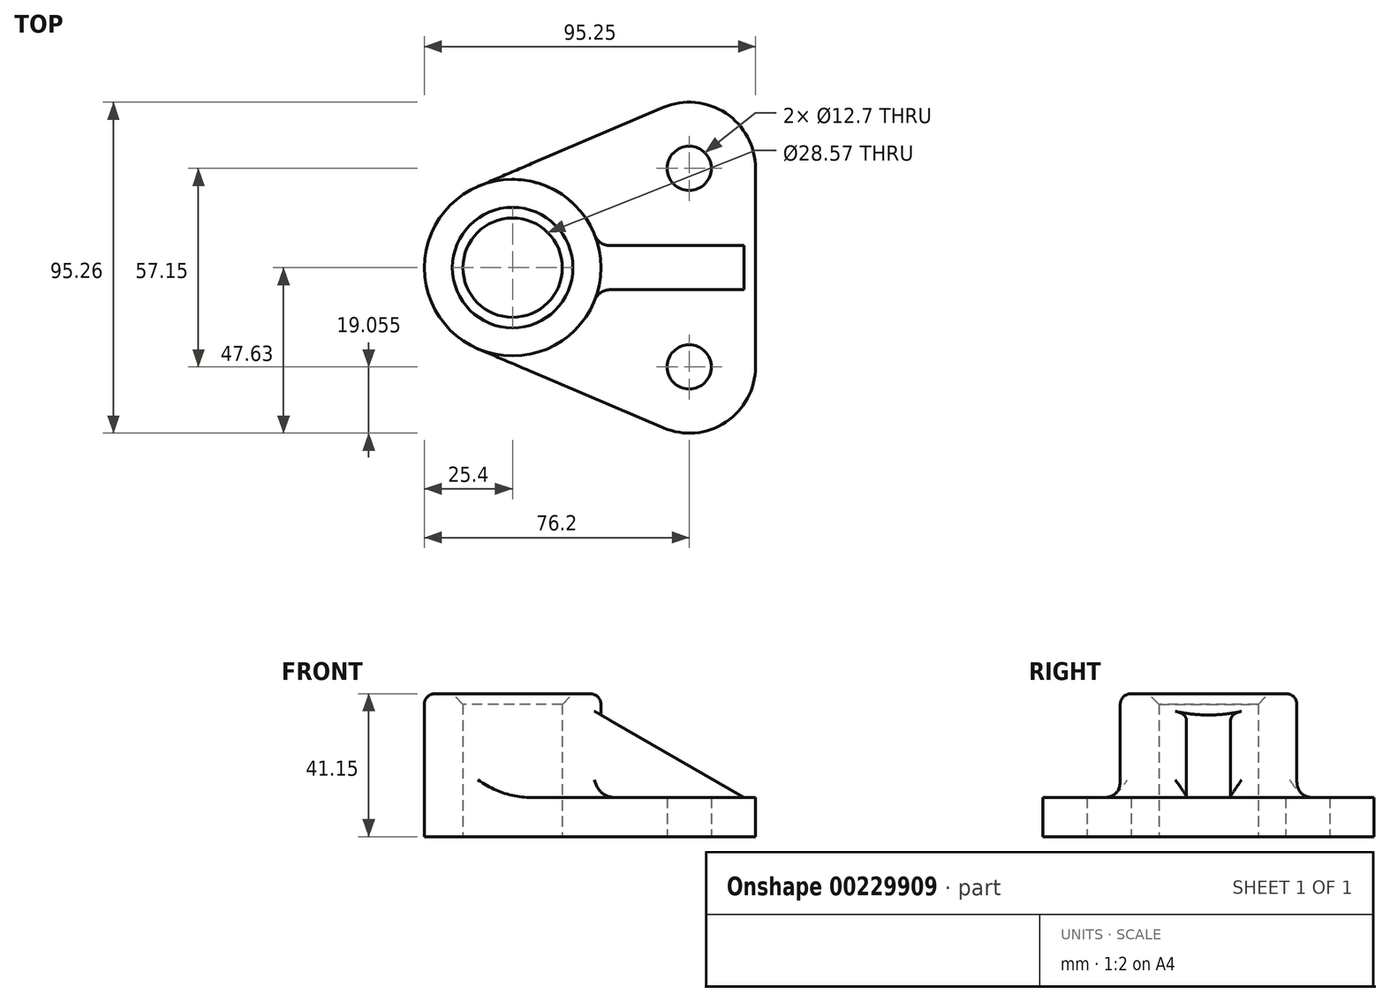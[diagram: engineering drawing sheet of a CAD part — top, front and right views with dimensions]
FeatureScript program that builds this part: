
annotation { "Feature Type Name" : "Feature", "Feature Type Description" : "" }
export const myFeature = defineFeature(function(context is Context, id is Id, definition is map)
    precondition{}
    {
        {
            var Q0;
            Q0=qCreatedBy(makeId("Top.planeOp"),FACE);
            var sketch = newSketch(context, id + "F0", { "sketchPlane" : qUnion([Q0])});
            skCircle(sketch, "E0", {"center": v(0, 0) * mm, "radius": 25.4 * mm});
            skCircle(sketch, "E1", {"center": v(0, 0) * mm, "radius": 14.29 * mm});
            skLineSegment(sketch, "E2", {"start": v(0, 0) * mm, "end": v(14.29, 0) * mm, "construction": true});
            skCircle(sketch, "E3", {"center": v(50.8, -28.58) * mm, "radius": 6.35 * mm});
            skCircle(sketch, "E4", {"center": v(50.8, 28.58) * mm, "radius": 6.35 * mm});
            skArc(sketch, "E5", {"start": v(69.85, 28.58) * mm, "mid": v(61.3, 44.47) * mm, "end": v(43.33, 46.1) * mm});
            skArc(sketch, "E6", {"start": v(43.33, -46.1) * mm, "mid": v(61.3, -44.47) * mm, "end": v(69.85, -28.58) * mm});
            skLineSegment(sketch, "E7", {"start": v(-9.97, 23.36) * mm, "end": v(43.33, 46.1) * mm});
            skLineSegment(sketch, "E8", {"start": v(-9.97, -23.36) * mm, "end": v(43.33, -46.1) * mm});
            skLineSegment(sketch, "E9", {"start": v(69.85, -28.58) * mm, "end": v(69.85, 28.58) * mm});
            skPoint(sketch, "E10.orphan", {"position": v(48.26, 0) * mm});
            skSolve(sketch);
        }
        {
            var Q0;
            Q0 = qSketchRegion(id + "F0", true);
            extrude(context, id + "F1", {"entities" : qUnion([Q0]), "depth" : 11.28 * mm});
        }
        {
            var Q0;
            Q0=makeQuery(id+"F0.imprint","IMPRINT",FACE,{"disambiguationData":[TD([[makeQuery(id+"F0.imprint","IMPRINT",EDGE,{"derivedFrom":sQuery(id+"F0.wireOp",EDGE,"E1")}),-1.0]])]});
            extrude(context, id + "F2", {"entities" : qUnion([Q0]), "operationType" : NewBodyOperationType.ADD, "depth" : 41.15 * mm});
        }
        {
            var Q0;
            Q0=qCreatedBy(makeId("Front.planeOp"),FACE);
            var sketch = newSketch(context, id + "F3", { "sketchPlane" : qUnion([Q0])});
            skLineSegment(sketch, "E11.0", {"start": v(43.33, 11.28) * mm, "end": v(69.85, 11.28) * mm});
            skLineSegment(sketch, "E12", {"start": v(66.55, 11.28) * mm, "end": v(25.4, 35.03) * mm});
            skLineSegment(sketch, "E13", {"start": v(43.33, 11.28) * mm, "end": v(25.4, 11.28) * mm});
            skLineSegment(sketch, "E14", {"start": v(17.7, 11.28) * mm, "end": v(25.4, 11.28) * mm});
            skLineSegment(sketch, "E15", {"start": v(25.4, 35.03) * mm, "end": v(17.7, 39.51) * mm});
            skLineSegment(sketch, "E16", {"start": v(17.7, 39.51) * mm, "end": v(17.7, 11.28) * mm});
            skSolve(sketch);
        }
        {
            var Q0;
            Q0 = qSketchRegion(id + "F3", true);
            extrude(context, id + "F4", {"entities" : qUnion([Q0]), "operationType" : NewBodyOperationType.ADD, "endBound" : BoundingType.SYMMETRIC, "depth" : 12.7 * mm});
        }
        {
            var Q0;
            {var subQ0=sQuery(id+"F0.wireOp",EDGE,"E0");var subQ1=makeQuery(id+"F2.opExtrude","SWEPT_FACE",FACE,{"disambiguationData":[OSD([subQ0])]});var subQ2=sQuery(id+"F0.wireOp",EDGE,"E8");var subQ3=makeQuery(id+"F1.opExtrude","CAP_FACE",FACE,{"disambiguationData":[OSD([subQ0,sQuery(id+"F0.wireOp",EDGE,"E1"),sQuery(id+"F0.wireOp",EDGE,"E3"),sQuery(id+"F0.wireOp",EDGE,"E4"),sQuery(id+"F0.wireOp",EDGE,"E5"),sQuery(id+"F0.wireOp",EDGE,"E6"),sQuery(id+"F0.wireOp",EDGE,"E7"),subQ2,sQuery(id+"F0.wireOp",EDGE,"E9")])],"isStart":false});Q0=makeQuery(id+"F4.boolean.opBoolean","SPLIT",EDGE,{"disambiguationData":[TD([makeQuery(id+"F1.opExtrude","SWEPT_FACE",FACE,{"disambiguationData":[OSD([subQ2])]})])],"derivedFrom":makeQuery(id+"F2.boolean.opBoolean","INTERSECT",EDGE,{"derivedFrom":[subQ3,subQ1]})});}
            var Q1;
            {var subQ0=sQuery(id+"F0.wireOp",EDGE,"E0");var subQ1=makeQuery(id+"F2.opExtrude","SWEPT_FACE",FACE,{"disambiguationData":[OSD([subQ0])]});var subQ2=sQuery(id+"F0.wireOp",EDGE,"E7");var subQ3=makeQuery(id+"F1.opExtrude","CAP_FACE",FACE,{"disambiguationData":[OSD([subQ0,sQuery(id+"F0.wireOp",EDGE,"E1"),sQuery(id+"F0.wireOp",EDGE,"E3"),sQuery(id+"F0.wireOp",EDGE,"E4"),sQuery(id+"F0.wireOp",EDGE,"E5"),sQuery(id+"F0.wireOp",EDGE,"E6"),subQ2,sQuery(id+"F0.wireOp",EDGE,"E8"),sQuery(id+"F0.wireOp",EDGE,"E9")])],"isStart":false});Q1=makeQuery(id+"F4.boolean.opBoolean","SPLIT",EDGE,{"disambiguationData":[TD([makeQuery(id+"F1.opExtrude","SWEPT_FACE",FACE,{"disambiguationData":[OSD([subQ2])]})])],"derivedFrom":makeQuery(id+"F2.boolean.opBoolean","INTERSECT",EDGE,{"derivedFrom":[subQ3,subQ1]})});}
            var Q2;
            {var subQ0=sQuery(id+"F0.wireOp",EDGE,"E0");Q2=makeQuery(id+"F4.boolean.opBoolean","INTERSECT",EDGE,{"derivedFrom":[makeQuery(id+"F2.boolean.opBoolean","MERGE",FACE,{"derivedFrom":[makeQuery(id+"F1.opExtrude","SWEPT_FACE",FACE,{"disambiguationData":[OSD([subQ0])]}),makeQuery(id+"F2.opExtrude","SWEPT_FACE",FACE,{"disambiguationData":[OSD([subQ0])]})]}),makeQuery(id+"F4.opExtrude","CAP_FACE",FACE,{"disambiguationData":[OSD([sQuery(id+"F3.wireOp",EDGE,"E11.0"),sQuery(id+"F3.wireOp",EDGE,"E12"),sQuery(id+"F3.wireOp",EDGE,"E13"),sQuery(id+"F3.wireOp",EDGE,"E14"),sQuery(id+"F3.wireOp",EDGE,"E15"),sQuery(id+"F3.wireOp",EDGE,"E16")])],"isStart":false})]});}
            var Q3;
            Q3=makeQuery(id+"F4.opExtrude","CAP_EDGE",EDGE,{"disambiguationData":[OSD([sQuery(id+"F3.wireOp",EDGE,"E11.0"),sQuery(id+"F3.wireOp",EDGE,"E13"),sQuery(id+"F3.wireOp",EDGE,"E14")])],"isStart":false});
            var Q4;
            {var subQ0=sQuery(id+"F0.wireOp",EDGE,"E0");Q4=makeQuery(id+"F4.boolean.opBoolean","INTERSECT",EDGE,{"derivedFrom":[makeQuery(id+"F2.boolean.opBoolean","MERGE",FACE,{"derivedFrom":[makeQuery(id+"F1.opExtrude","SWEPT_FACE",FACE,{"disambiguationData":[OSD([subQ0])]}),makeQuery(id+"F2.opExtrude","SWEPT_FACE",FACE,{"disambiguationData":[OSD([subQ0])]})]}),makeQuery(id+"F4.opExtrude","CAP_FACE",FACE,{"disambiguationData":[OSD([sQuery(id+"F3.wireOp",EDGE,"E11.0"),sQuery(id+"F3.wireOp",EDGE,"E12"),sQuery(id+"F3.wireOp",EDGE,"E13"),sQuery(id+"F3.wireOp",EDGE,"E14"),sQuery(id+"F3.wireOp",EDGE,"E15"),sQuery(id+"F3.wireOp",EDGE,"E16")])],"isStart":true})]});}
            var Q5;
            Q5=makeQuery(id+"F4.opExtrude","CAP_EDGE",EDGE,{"disambiguationData":[OSD([sQuery(id+"F3.wireOp",EDGE,"E11.0"),sQuery(id+"F3.wireOp",EDGE,"E13"),sQuery(id+"F3.wireOp",EDGE,"E14")])],"isStart":true});
            fillet(context, id + "F5", {"entities" : qUnion([Q0, Q1, Q2, Q3, Q4, Q5]), "radius" : 5.08 * mm, "rho" : 0.5, "crossSection" : FilletCrossSection.CONIC, "allowEdgeOverflow" : false});
        }
        {
            var Q0;
            Q0=makeQuery(id+"F2.opExtrude","CAP_EDGE",EDGE,{"disambiguationData":[OSD([sQuery(id+"F0.wireOp",EDGE,"E0")])],"isStart":false});
            fillet(context, id + "F6", {"entities" : qUnion([Q0]), "radius" : 3.05 * mm, "tangentPropagation" : true, "allowEdgeOverflow" : false});
        }
        {
            var Q0;
            Q0=makeQuery(id+"F2.opExtrude","CAP_EDGE",EDGE,{"disambiguationData":[OSD([sQuery(id+"F0.wireOp",EDGE,"E1")])],"isStart":false});
            chamfer(context, id + "F7", {"entities" : qUnion([Q0]), "width" : 3.05 * mm, "tangentPropagation" : true});
        }
    });
